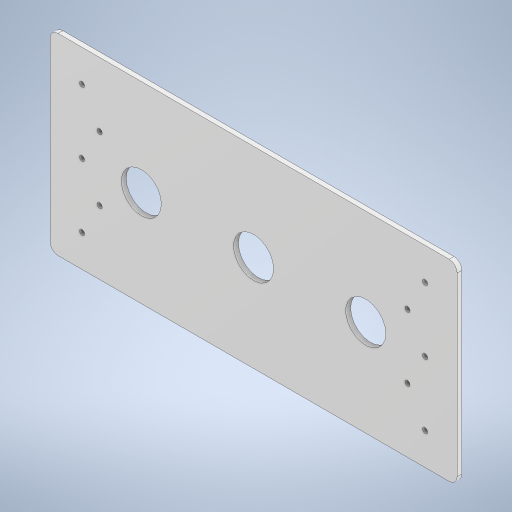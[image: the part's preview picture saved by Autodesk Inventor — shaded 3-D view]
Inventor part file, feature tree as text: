
AUTODESK INVENTOR PART (.ipt)
format: ipt  version: 2024.3 (Build 283343000, 343)  size: 292,352 bytes
history: native  units: mm
features: sketch x5, extrude x4, other x1, fillet x1, hole x1
ambient origin geometry x8: Origin, YZ Plane, XZ Plane, XY Plane, X Axis, Y Axis, Z Axis, Center Point
bodies: Body1 (feature_tree)
feature tree (12):
  other  "ソリッド1"
  extrude  "押し出し1"  Depth=260.0mm
  extrude  "押し出し3"  Depth=3.0mm
  extrude  "押し出し4"  Depth=120.0mm TaperAngle=0.0deg
  extrude  "押し出し7"  Depth=25.0mm
  fillet  "フィレット1"  Radius=25.0mm
  hole  "穴1"  [1 undecoded]
  sketch  "スケッチ1"
  sketch  "スケッチ3"
  sketch  "スケッチ5"
  sketch  "スケッチ8"
  sketch  "スケッチ13"
note: 1 required parameter value undecoded (feature->parameter linkage not recoverable at this tier; creation-order binding heuristic only, values carry confidence <= 0.55)
